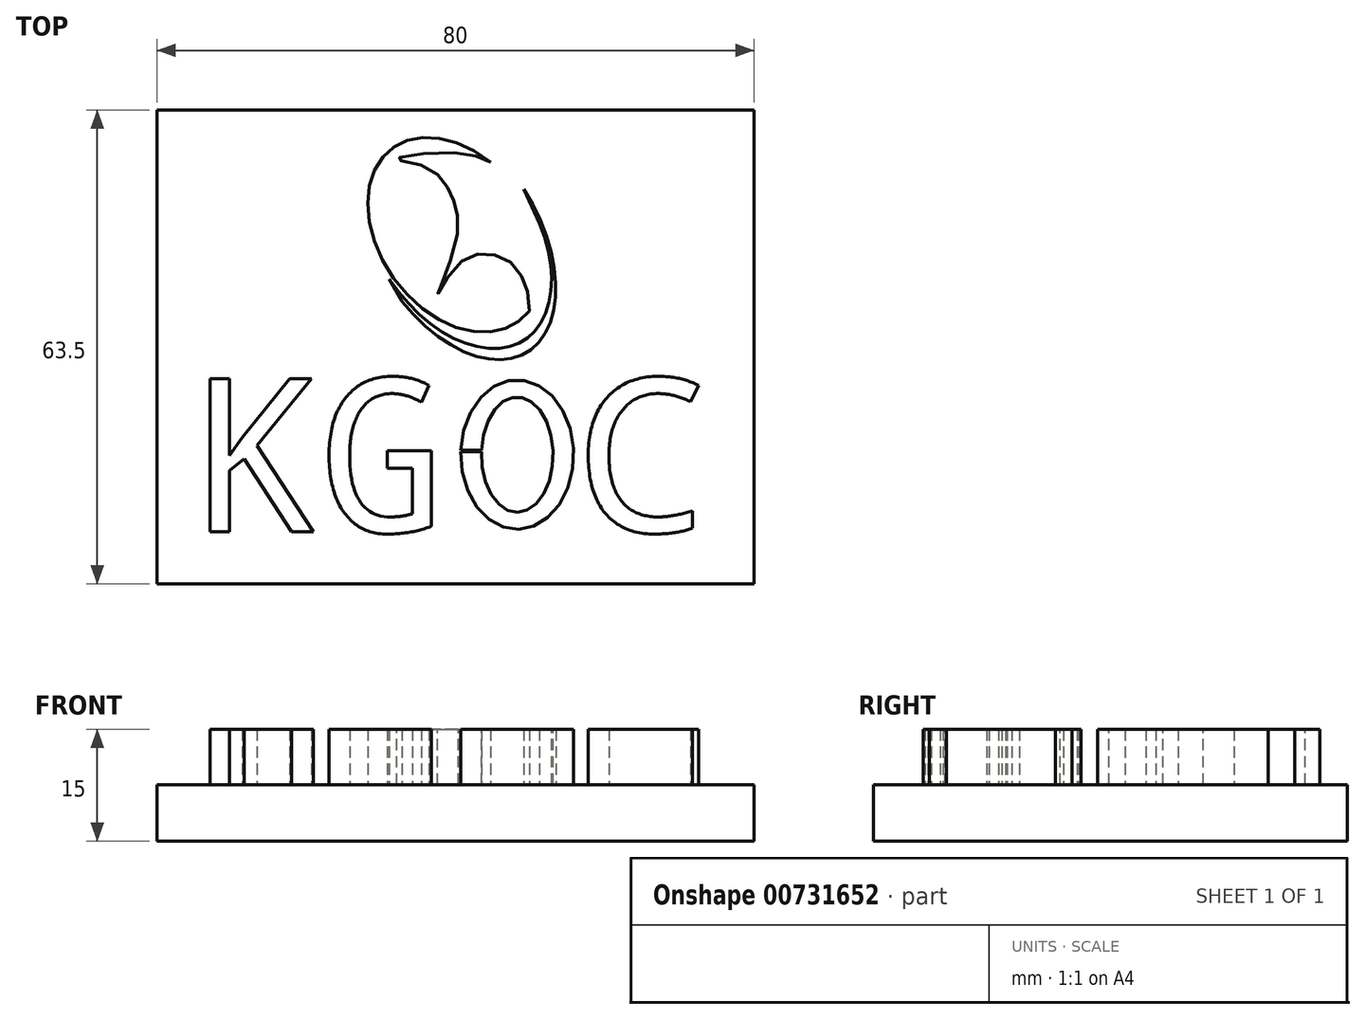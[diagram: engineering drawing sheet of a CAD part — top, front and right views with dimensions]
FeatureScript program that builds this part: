
annotation { "Feature Type Name" : "Feature", "Feature Type Description" : "" }
export const myFeature = defineFeature(function(context is Context, id is Id, definition is map)
    precondition{}
    {
        {
            var Q0;
            Q0=qCreatedBy(makeId("Top.planeOp"),FACE);
            var sketch = newSketch(context, id + "F0", { "sketchPlane" : qUnion([Q0])});
            skLineSegment(sketch, "E0.bottom", {"start": v(40, -33.5) * mm, "end": v(-40, -33.5) * mm});
            skLineSegment(sketch, "E0.top", {"start": v(40, 30) * mm, "end": v(-40, 30) * mm});
            skLineSegment(sketch, "E0.left", {"start": v(40, -30) * mm, "end": v(40, 30) * mm});
            skLineSegment(sketch, "E0.right", {"start": v(-40, -30) * mm, "end": v(-40, 30) * mm});
            skPoint(sketch, "E0.middle", {"position": v(0, 0) * mm});
            skLineSegment(sketch, "E1", {"start": v(-40, -32.5) * mm, "end": v(-40, -30) * mm});
            skLineSegment(sketch, "E2", {"start": v(40, -32.5) * mm, "end": v(40, -30) * mm});
            skLineSegment(sketch, "E3", {"start": v(-40, -33.5) * mm, "end": v(-40, -32.5) * mm});
            skLineSegment(sketch, "E4", {"start": v(40, -33.5) * mm, "end": v(40, -32.5) * mm});
            skSolve(sketch);
        }
        {
            var Q0;
            Q0=qCreatedBy(makeId("Top.planeOp"),FACE);
            var sketch = newSketch(context, id + "F1", { "sketchPlane" : qUnion([Q0])});
            skLineSegment(sketch, "E5.bottom", {"start": v(40, 30) * mm, "end": v(-40, 30) * mm});
            skLineSegment(sketch, "E5.top", {"start": v(40, -30) * mm, "end": v(-40, -30) * mm});
            skLineSegment(sketch, "E5.left", {"start": v(40, 30) * mm, "end": v(40, -30) * mm});
            skLineSegment(sketch, "E5.right", {"start": v(-40, 30) * mm, "end": v(-40, -30) * mm});
            skEllipticalArc(sketch, "E6", {});
            skFitSpline(sketch, "E7", {"points": [v(4.68, 22.98) * mm, v(0, 24.3) * mm, v(-7.9, 23.45) * mm, v(-4.3, 22.5) * mm, v(-1.14, 19.75) * mm, v(0, 17.07) * mm, v(0, 12) * mm, v(-2.41, 5.32) * mm, v(0, 9.01) * mm, v(3.99, 10.72) * mm, v(7.7, 9.33) * mm, v(9.6, 5.72) * mm, v(9.81, 4.1) * mm, v(9.88, 3.05) * mm], "startDerivative": vector(-41.73, 21.4) * mm, "endDerivative": vector(1.74, -26.45) * mm});
            skText(sketch, "E8", { "text": "KG C", "fontName": "DroidSansMono.ttf"});
            skEllipticalArc(sketch, "E9", {});
            skEllipticalArc(sketch, "E10", {});
            skLineSegment(sketch, "E11", {"start": v(0.71, -15.6) * mm, "end": v(3.48, -15.6) * mm});
            skLineSegment(sketch, "E12", {"start": v(0.7, -15.76) * mm, "end": v(3.47, -15.76) * mm});
            skEllipticalArc(sketch, "E13", {});
            skPoint(sketch, "E14", {"position": v(8.92, 19.16) * mm});
            skPoint(sketch, "E15", {"position": v(-8.86, 7.31) * mm});
            skPoint(sketch, "E15.positionSnap0", {"position": v(-8.2, 7.31) * mm});
            skLineSegment(sketch, "E16", {"start": v(-8.86, 7.31) * mm, "end": v(-8.86, 7.31) * mm});
            skEllipticalArc(sketch, "E17", {});
            skLineSegment(sketch, "E18", {"start": v(-8.86, 7.31) * mm, "end": v(-7.16, 4.34) * mm});
            skLineSegment(sketch, "E19", {"start": v(11.23, 14.82) * mm, "end": v(9.16, 19.41) * mm});
            const initialGuessF1  = {"E6": [0, 0.013280665501952171, 0.588047108010237, -0.8088266802973285, 0.014364267136818275, 0.010145458212735088, 1.933497985232494, 0.19599463424631375], "E8": [-0.03587, -0.02655, 1, 0, 0.02073], "E9": [0.008266090415418148, -0.016186440363526344, 0, -1, 0.010015109553933144, 0.007566245832075456, 4.669752922945587, 4.654139303713688], "E10": [0.008266090415418148, -0.016186440363526344, 0, -1, 0.007730962708592415, 0.0048037835103717265, 4.657144549083569, 4.636900170979201], "E13": [0, 0.013280665624082779, 0.5504902227555601, -0.8348416105169495, 0.016848362782801576, 0.01068347433884253, 4.718429698237844, 1.276235269732398], "E17": [0, 0.013280665501952171, 0.5202883685116907, -0.8539906402247295, 0.018430770766502246, 0.011018020164653057, 4.9263685747038695, 1.5962880306640583]};
            skSetInitialGuess(sketch, initialGuessF1);
            skSolve(sketch);
        }
        {
            var Q0;
            Q0=makeQuery(id+"F1.imprint","IMPRINT",FACE,{"disambiguationData":[TD([[makeQuery(id+"F1.imprint","IMPRINT",EDGE,{"derivedFrom":sQuery(id+"F1.wireOp",EDGE,"E8.sketch_text.stroke-30")}),-1.0]])]});
            var Q1;
            Q1=makeQuery(id+"F1.imprint","IMPRINT",FACE,{"disambiguationData":[TD([[makeQuery(id+"F1.imprint","IMPRINT",EDGE,{"derivedFrom":sQuery(id+"F1.wireOp",EDGE,"E8.sketch_text.stroke-13")}),-1.0]])]});
            var Q2;
            Q2=makeQuery(id+"F1.imprint","IMPRINT",FACE,{"disambiguationData":[TD([[makeQuery(id+"F1.imprint","IMPRINT",EDGE,{"derivedFrom":sQuery(id+"F1.wireOp",EDGE,"E8.sketch_text.stroke-0")}),-1.0]])]});
            var Q3;
            Q3=makeQuery(id+"F1.imprint","IMPRINT",FACE,{"disambiguationData":[TD([[makeQuery(id+"F1.imprint","IMPRINT",EDGE,{"derivedFrom":sQuery(id+"F1.wireOp",EDGE,"E9")}),1.0]])]});
            var Q4;
            Q4=makeQuery(id+"F1.imprint","IMPRINT",FACE,{"disambiguationData":[TD([[makeQuery(id+"F1.imprint","IMPRINT",EDGE,{"derivedFrom":sQuery(id+"F1.wireOp",EDGE,"E6")}),1.0]])]});
            var Q5;
            Q5=makeQuery(id+"F1.imprint","IMPRINT",FACE,{"disambiguationData":[TD([[makeQuery(id+"F1.imprint","IMPRINT",EDGE,{"derivedFrom":sQuery(id+"F1.wireOp",EDGE,"E13")}),-1.0]])]});
            extrude(context, id + "F2", {"entities" : qUnion([Q0, Q1, Q2, Q3, Q4, Q5]), "depth" : 7.5 * mm, "offsetDistance" : 25 * mm});
        }
        {
            var Q0;
            Q0 = qSketchRegion(id + "F0", true);
            extrude(context, id + "F3", {"entities" : qUnion([Q0]), "operationType" : NewBodyOperationType.ADD, "depth" : 0.1 * mm, "offsetDistance" : 25 * mm, "hasSecondDirection" : true, "secondDirectionOppositeDirection" : true, "secondDirectionDepth" : 7.5 * mm});
        }
    });
